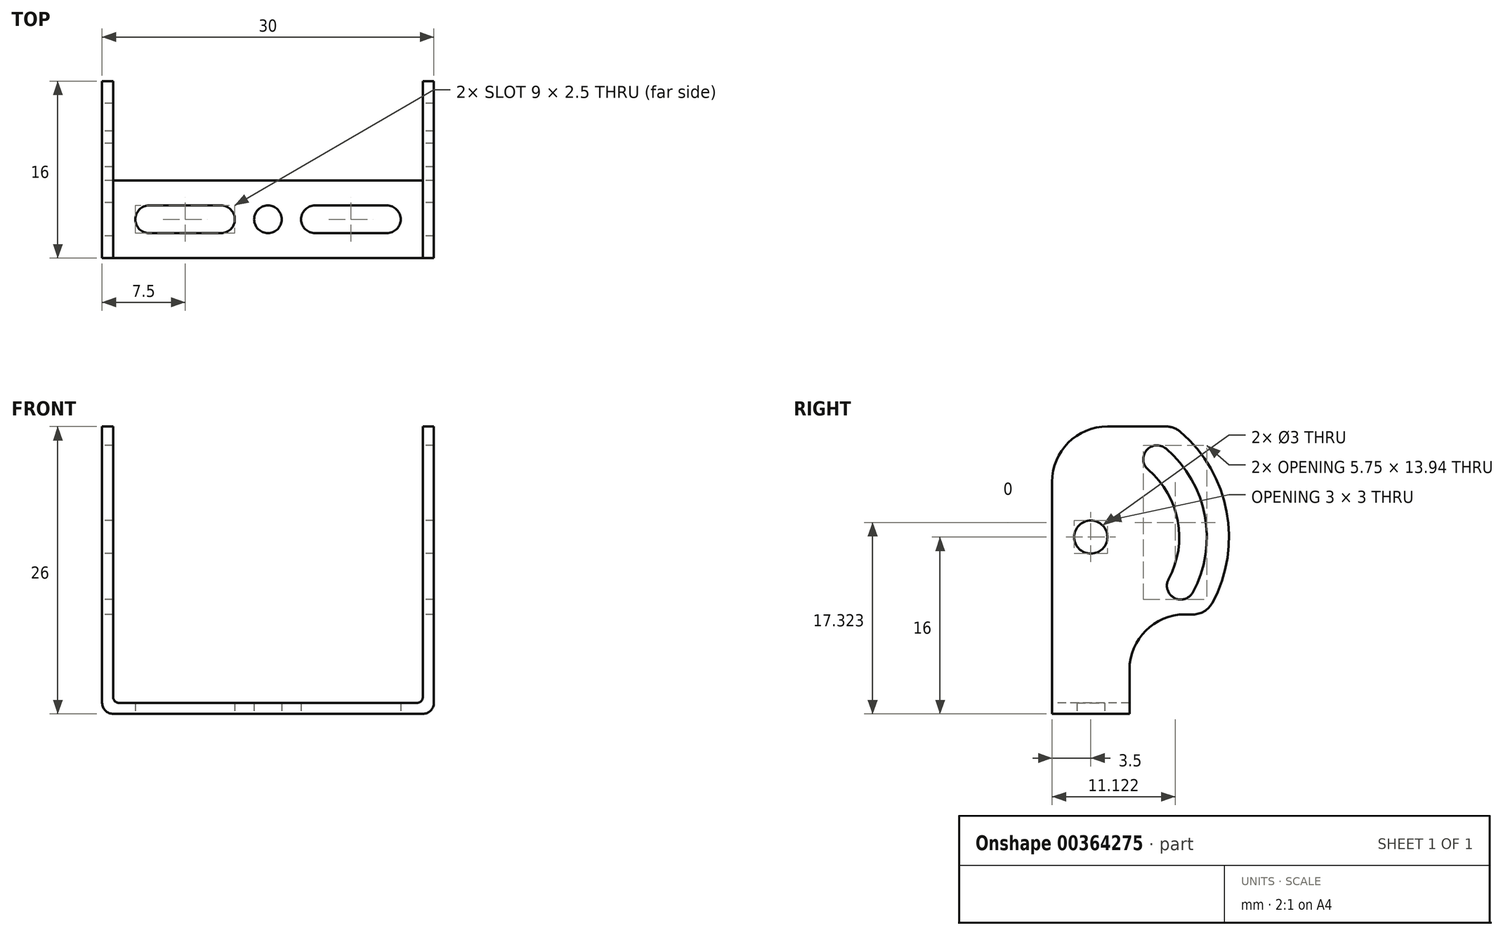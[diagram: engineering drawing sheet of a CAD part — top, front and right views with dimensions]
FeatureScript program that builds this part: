
annotation { "Feature Type Name" : "Feature", "Feature Type Description" : "" }
export const myFeature = defineFeature(function(context is Context, id is Id, definition is map)
    precondition{}
    {
        {
            var Q0;
            Q0=qCreatedBy(makeId("Right.planeOp"),FACE);
            var sketch = newSketch(context, id + "F0", { "sketchPlane" : qUnion([Q0])});
            skLineSegment(sketch, "E0.bottom", {"start": v(-3.5, 0) * mm, "end": v(3.5, 0) * mm});
            skLineSegment(sketch, "E0.top", {"start": v(1.5, 26) * mm, "end": v(6.8, 26) * mm});
            skLineSegment(sketch, "E0.left", {"start": v(-3.5, 0) * mm, "end": v(-3.5, 21) * mm});
            skCircle(sketch, "E1", {"center": v(0, 16) * mm, "radius": 1.5 * mm});
            skPoint(sketch, "E2.visualSharp", {"position": v(-3.5, 26) * mm});
            skArc(sketch, "E2.filletArc", {"start": v(1.5, 26) * mm, "mid": v(-2.04, 24.54) * mm, "end": v(-3.5, 21) * mm});
            skArc(sketch, "E3", {"start": v(11, 10.05) * mm, "mid": v(12.29, 18.3) * mm, "end": v(8.1, 25.52) * mm});
            skLineSegment(sketch, "E4", {"start": v(9.23, 9) * mm, "end": v(8.5, 9) * mm});
            skLineSegment(sketch, "E5", {"start": v(3.5, 4) * mm, "end": v(3.5, 0) * mm});
            skPoint(sketch, "E6.visualSharp", {"position": v(7.5, 26) * mm});
            skArc(sketch, "E6.filletArc", {"start": v(8.1, 25.52) * mm, "mid": v(7.5, 25.88) * mm, "end": v(6.8, 26) * mm});
            skPoint(sketch, "E7.visualSharp", {"position": v(10.36, 9) * mm});
            skArc(sketch, "E7.filletArc", {"start": v(9.23, 9) * mm, "mid": v(10.26, 9.28) * mm, "end": v(11, 10.05) * mm});
            skPoint(sketch, "E8.visualSharp", {"position": v(3.5, 9) * mm});
            skArc(sketch, "E8.filletArc", {"start": v(8.5, 9) * mm, "mid": v(4.96, 7.54) * mm, "end": v(3.5, 4) * mm});
            skArc(sketch, "E9.0", {"start": v(9.23, 11) * mm, "mid": v(10.32, 17.93) * mm, "end": v(6.8, 24) * mm});
            skArc(sketch, "E10.0", {"start": v(7.03, 12.2) * mm, "mid": v(7.86, 17.47) * mm, "end": v(5.18, 22.1) * mm});
            skArc(sketch, "E11", {"start": v(6.8, 24) * mm, "mid": v(5.04, 23.86) * mm, "end": v(5.18, 22.1) * mm});
            skArc(sketch, "E12", {"start": v(7.03, 12.2) * mm, "mid": v(7.54, 10.5) * mm, "end": v(9.23, 11) * mm});
            skLineSegment(sketch, "E13", {"start": v(7.03, 12.2) * mm, "end": v(9.23, 11) * mm, "construction": true});
            skLineSegment(sketch, "E14", {"start": v(6.8, 24) * mm, "end": v(5.18, 22.1) * mm, "construction": true});
            skLineSegment(sketch, "E15", {"start": v(0, 16) * mm, "end": v(7.03, 12.2) * mm, "construction": true});
            skLineSegment(sketch, "E16", {"start": v(0, 16) * mm, "end": v(5.18, 22.1) * mm, "construction": true});
            skSolve(sketch);
        }
        {
            var Q0;
            Q0 = qSketchRegion(id + "F0", true);
            extrude(context, id + "F1", {"entities" : qUnion([Q0]), "endBound" : BoundingType.SYMMETRIC, "depth" : 30 * mm});
        }
        {
            var Q0;
            Q0=makeQuery(id+"F1.opExtrude","SWEPT_FACE",FACE,{"disambiguationData":[OSD([sQuery(id+"F0.wireOp",EDGE,"E0.left")])]});
            var sketch = newSketch(context, id + "F2", { "sketchPlane" : qUnion([Q0])});
            skLineSegment(sketch, "E17.bottom", {"start": v(-14, 26) * mm, "end": v(14, 26) * mm});
            skLineSegment(sketch, "E17.top", {"start": v(-13.5, 1) * mm, "end": v(13.5, 1) * mm});
            skLineSegment(sketch, "E17.left", {"start": v(-14, 26) * mm, "end": v(-14, 1.5) * mm});
            skLineSegment(sketch, "E17.right", {"start": v(14, 26) * mm, "end": v(14, 1.5) * mm});
            skPoint(sketch, "E18.visualSharp", {"position": v(-14, 1) * mm});
            skArc(sketch, "E18.filletArc", {"start": v(-14, 1.5) * mm, "mid": v(-13.85, 1.15) * mm, "end": v(-13.5, 1) * mm});
            skPoint(sketch, "E19.visualSharp", {"position": v(14, 1) * mm});
            skArc(sketch, "E19.filletArc", {"start": v(13.5, 1) * mm, "mid": v(13.85, 1.15) * mm, "end": v(14, 1.5) * mm});
            skSolve(sketch);
        }
        {
            var Q0;
            Q0 = qSketchRegion(id + "F2", true);
            extrude(context, id + "F3", {"entities" : qUnion([Q0]), "operationType" : NewBodyOperationType.REMOVE, "oppositeDirection" : true, "depth" : 25 * mm});
        }
        {
            var Q0;
            Q0=makeQuery(id+"F1.opExtrude","CAP_EDGE",EDGE,{"disambiguationData":[OSD([sQuery(id+"F0.wireOp",EDGE,"E0.bottom")])],"isStart":true});
            var Q1;
            Q1=makeQuery(id+"F1.opExtrude","CAP_EDGE",EDGE,{"disambiguationData":[OSD([sQuery(id+"F0.wireOp",EDGE,"E0.bottom")])],"isStart":false});
            fillet(context, id + "F4", {"entities" : qUnion([Q0, Q1]), "radius" : 1 * mm, "tangentPropagation" : true, "allowEdgeOverflow" : false});
        }
        {
            var Q0;
            Q0=makeQuery(id+"F1.opExtrude","SWEPT_FACE",FACE,{"disambiguationData":[OSD([sQuery(id+"F0.wireOp",EDGE,"E0.bottom")])]});
            var sketch = newSketch(context, id + "F5", { "sketchPlane" : qUnion([Q0])});
            skCircle(sketch, "E20", {"center": v(0, 0) * mm, "radius": 1.25 * mm});
            skLineSegment(sketch, "E21", {"start": v(-10.75, 0) * mm, "end": v(-4.25, 0) * mm, "construction": true});
            skArc(sketch, "E22.0.startCap", {"start": v(-10.75, -1.25) * mm, "mid": v(-12, 0) * mm, "end": v(-10.75, 1.25) * mm});
            skArc(sketch, "E22.0.endCap", {"start": v(-4.25, 1.25) * mm, "mid": v(-3, 0) * mm, "end": v(-4.25, -1.25) * mm});
            skLineSegment(sketch, "E22.0.left", {"start": v(-10.75, 1.25) * mm, "end": v(-4.25, 1.25) * mm});
            skLineSegment(sketch, "E22.0.right", {"start": v(-10.75, -1.25) * mm, "end": v(-4.25, -1.25) * mm});
            skLineSegment(sketch, "E23.MirrorCS", {"start": v(10.75, 1.25) * mm, "end": v(4.25, 1.25) * mm});
            skArc(sketch, "E24.MirrorCS", {"start": v(4.25, 1.25) * mm, "mid": v(3, 0) * mm, "end": v(4.25, -1.25) * mm});
            skLineSegment(sketch, "E25.MirrorCS", {"start": v(10.75, -1.25) * mm, "end": v(4.25, -1.25) * mm});
            skArc(sketch, "E26.MirrorCS", {"start": v(10.75, -1.25) * mm, "mid": v(12, 0) * mm, "end": v(10.75, 1.25) * mm});
            skSolve(sketch);
        }
        {
            var Q0;
            Q0 = qSketchRegion(id + "F5", true);
            extrude(context, id + "F6", {"entities" : qUnion([Q0]), "operationType" : NewBodyOperationType.REMOVE, "oppositeDirection" : true, "depth" : 25 * mm});
        }
    });
